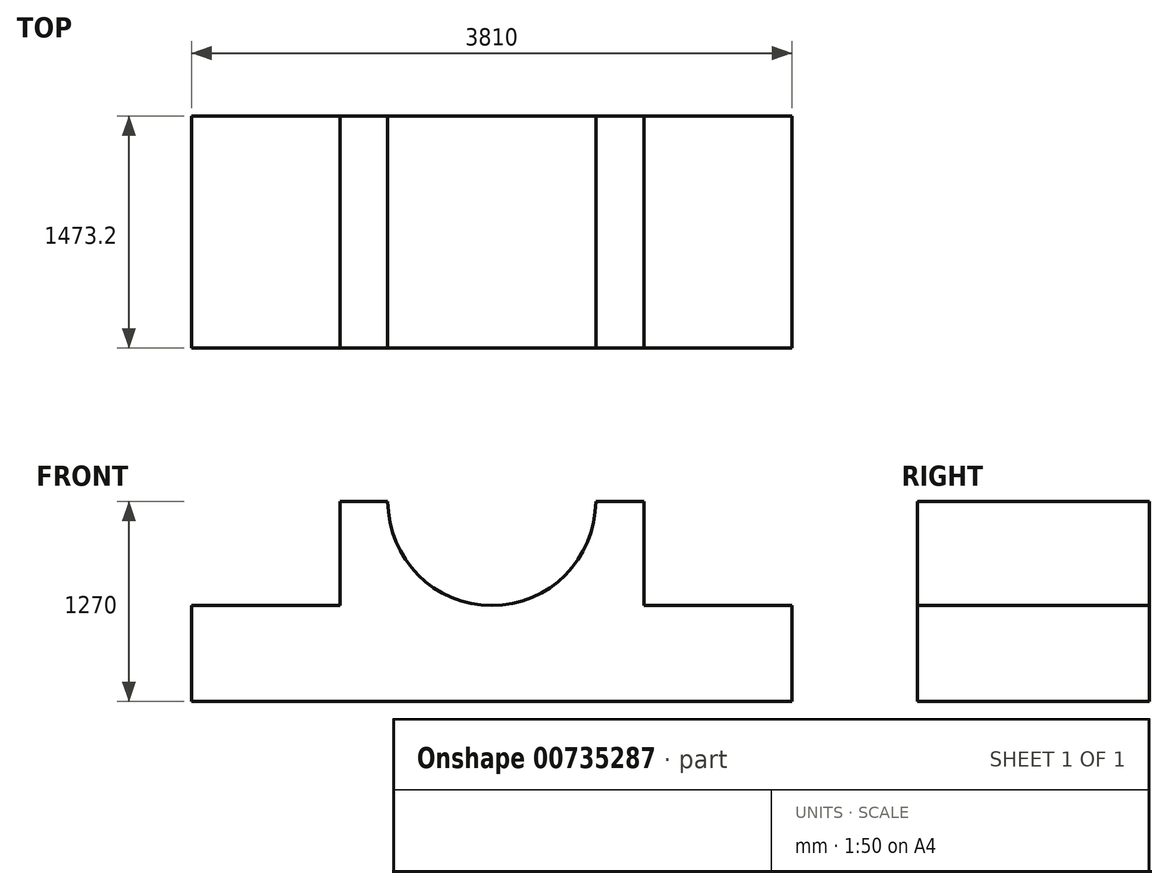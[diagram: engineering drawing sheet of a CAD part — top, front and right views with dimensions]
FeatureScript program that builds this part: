
annotation { "Feature Type Name" : "Feature", "Feature Type Description" : "" }
export const myFeature = defineFeature(function(context is Context, id is Id, definition is map)
    precondition{}
    {
        {
            var Q0;
            Q0=qCreatedBy(makeId("Front.planeOp"),FACE);
            var sketch = newSketch(context, id + "F0", { "sketchPlane" : qUnion([Q0])});
            skLineSegment(sketch, "E0.bottom", {"start": v(495.87, 1351.7) * mm, "end": v(2426.27, 1351.7) * mm});
            skLineSegment(sketch, "E0.top", {"start": v(495.87, 81.7) * mm, "end": v(2426.27, 81.7) * mm});
            skLineSegment(sketch, "E0.left", {"start": v(495.87, 1351.7) * mm, "end": v(495.87, 81.7) * mm});
            skLineSegment(sketch, "E0.right", {"start": v(2426.27, 1351.7) * mm, "end": v(2426.27, 81.7) * mm});
            skLineSegment(sketch, "E1.bottom", {"start": v(-443.93, 691.3) * mm, "end": v(3366.07, 691.3) * mm});
            skLineSegment(sketch, "E1.top", {"start": v(-443.93, 81.7) * mm, "end": v(3366.07, 81.7) * mm});
            skLineSegment(sketch, "E1.left", {"start": v(-443.93, 691.3) * mm, "end": v(-443.93, 81.7) * mm});
            skLineSegment(sketch, "E1.right", {"start": v(3366.07, 691.3) * mm, "end": v(3366.07, 81.7) * mm});
            skSolve(sketch);
        }
        {
            var Q0;
            {var subQ0=sQuery(id+"F0.wireOp",EDGE,"E0.bottom");Q0=makeQuery(id+"F0.imprint","IMPRINT",FACE,{"disambiguationData":[TD([[makeQuery(id+"F0.imprint","IMPRINT",EDGE,{"derivedFrom":subQ0}),-1.0]])]});}
            var Q1;
            {var subQ0=sQuery(id+"F0.wireOp",EDGE,"E1.top");var subQ1=sQuery(id+"F0.wireOp",EDGE,"E0.left");var subQ2=makeQuery(id+"F0.imprint","INTERSECT",VERTEX,{"derivedFrom":[subQ1,subQ0]});Q1=makeQuery(id+"F0.imprint","IMPRINT",FACE,{"disambiguationData":[TD([[makeQuery(id+"F0.imprint","IMPRINT",EDGE,{"disambiguationData":[TD([[subQ2,1.0]])],"derivedFrom":subQ1}),1.0]])]});}
            var Q2;
            {var subQ5=sQuery(id+"F0.wireOp",EDGE,"E1.left");Q2=makeQuery(id+"F0.imprint","IMPRINT",FACE,{"disambiguationData":[TD([[makeQuery(id+"F0.imprint","IMPRINT",EDGE,{"derivedFrom":subQ5}),1.0]])]});}
            var Q3;
            {var subQ5=sQuery(id+"F0.wireOp",EDGE,"E1.right");Q3=makeQuery(id+"F0.imprint","IMPRINT",FACE,{"disambiguationData":[TD([[makeQuery(id+"F0.imprint","IMPRINT",EDGE,{"derivedFrom":subQ5}),-1.0]])]});}
            extrude(context, id + "F1", {"entities" : qUnion([Q0, Q1, Q2, Q3]), "depth" : 1473.2 * mm, "offsetDistance" : 25.4 * mm});
        }
        {
            var Q0;
            Q0=makeQuery(id+"F1.opExtrude","CAP_FACE",FACE,{"disambiguationData":[OSD([sQuery(id+"F0.wireOp",EDGE,"E0.bottom"),sQuery(id+"F0.wireOp",EDGE,"E0.left"),sQuery(id+"F0.wireOp",EDGE,"E0.right"),sQuery(id+"F0.wireOp",EDGE,"E1.bottom"),sQuery(id+"F0.wireOp",EDGE,"E1.top"),sQuery(id+"F0.wireOp",EDGE,"E1.left"),sQuery(id+"F0.wireOp",EDGE,"E1.right")])],"isStart":false});
            var sketch = newSketch(context, id + "F2", { "sketchPlane" : qUnion([Q0])});
            skCircle(sketch, "E2", {"center": v(1461.07, 1351.7) * mm, "radius": 660.4 * mm});
            skSolve(sketch);
        }
        {
            var Q0;
            {var subQ0=sQuery(id+"F2.wireOp",EDGE,"E2");var subQ1=makeQuery(id+"F1.opExtrude","CAP_EDGE",EDGE,{"disambiguationData":[OSD([sQuery(id+"F0.wireOp",EDGE,"E0.bottom")])],"isStart":false});var subQ2=makeQuery(id+"F2.imprint","INTERSECT",VERTEX,{"disambiguationData":[OD(0.0)],"derivedFrom":[subQ1,subQ0]});Q0=makeQuery(id+"F2.imprint","IMPRINT",FACE,{"disambiguationData":[TD([[makeQuery(id+"F2.imprint","IMPRINT",EDGE,{"disambiguationData":[TD([[subQ2,-1.0]])],"derivedFrom":subQ0}),1.0]])]});}
            extrude(context, id + "F3", {"entities" : qUnion([Q0]), "operationType" : NewBodyOperationType.REMOVE, "oppositeDirection" : true, "depth" : 1574.8 * mm, "offsetDistance" : 25.4 * mm});
        }
    });
